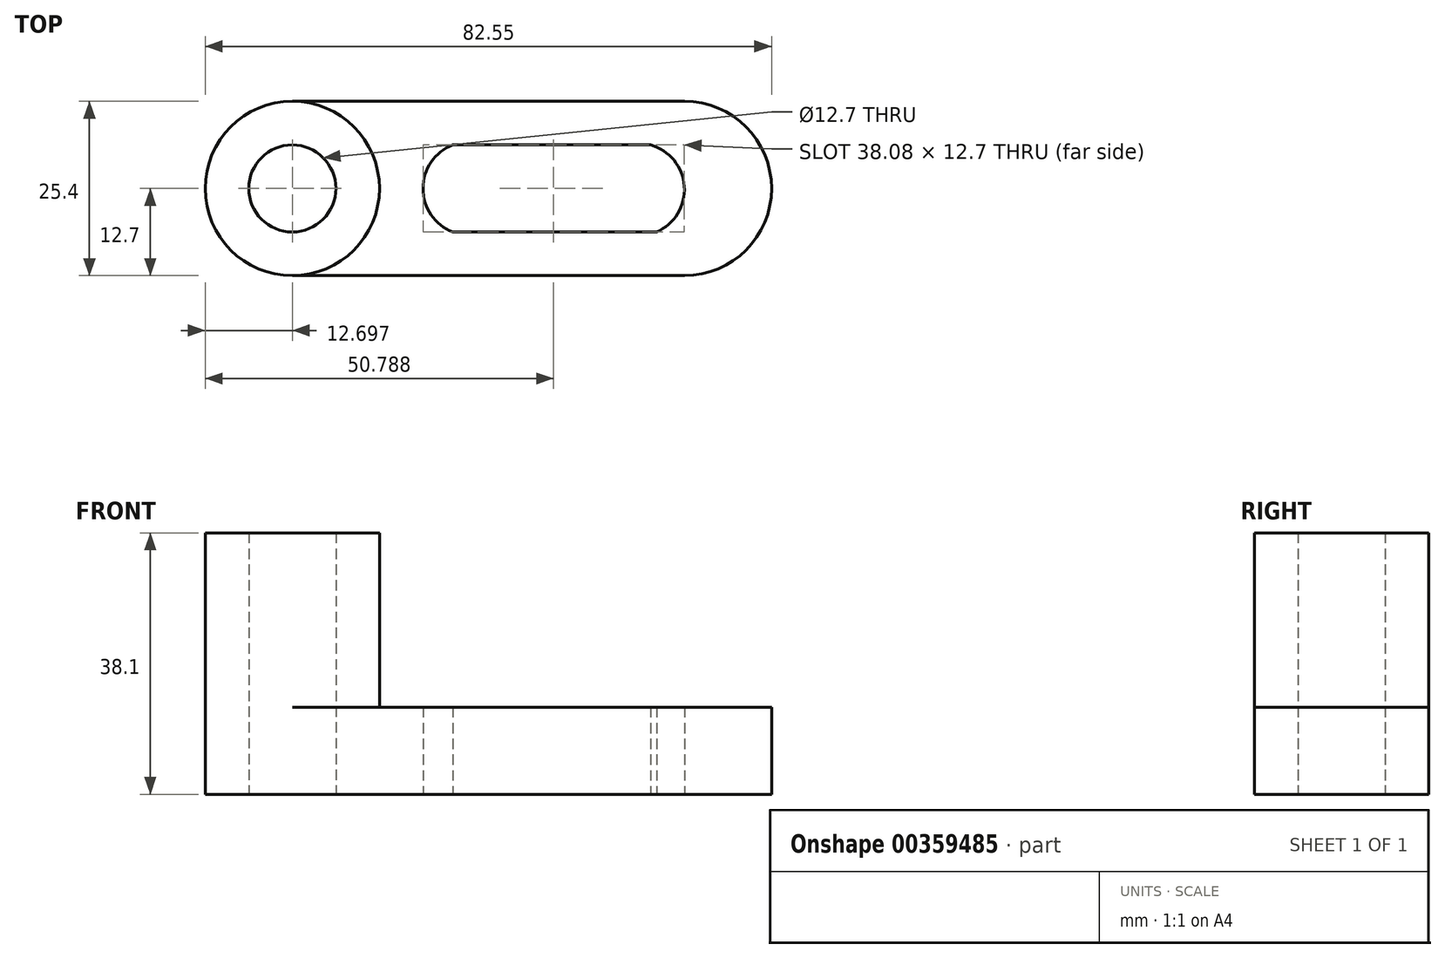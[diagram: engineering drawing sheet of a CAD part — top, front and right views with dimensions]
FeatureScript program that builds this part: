
annotation { "Feature Type Name" : "Feature", "Feature Type Description" : "" }
export const myFeature = defineFeature(function(context is Context, id is Id, definition is map)
    precondition{}
    {
        {
            var Q0;
            Q0=qCreatedBy(makeId("Front.planeOp"),FACE);
            var sketch = newSketch(context, id + "F0", { "sketchPlane" : qUnion([Q0])});
            skLineSegment(sketch, "E0", {"start": v(-36.1, 38.1) * mm, "end": v(-36.1, 0) * mm});
            skLineSegment(sketch, "E1", {"start": v(-36.1, 0) * mm, "end": v(46.46, 0) * mm});
            skLineSegment(sketch, "E2", {"start": v(46.46, 0) * mm, "end": v(46.46, 38.1) * mm});
            skLineSegment(sketch, "E3", {"start": v(46.46, 38.1) * mm, "end": v(-36.1, 38.1) * mm});
            skSolve(sketch);
        }
        {
            var Q0;
            Q0 = qSketchRegion(id + "F0", true);
            extrude(context, id + "F1", {"entities" : qUnion([Q0]), "oppositeDirection" : true, "depth" : 25.4 * mm});
        }
        {
            var Q0;
            Q0=qCreatedBy(makeId("Front.planeOp"),FACE);
            var sketch = newSketch(context, id + "F2", { "sketchPlane" : qUnion([Q0])});
            skLineSegment(sketch, "E4", {"start": v(-10.7, 38.1) * mm, "end": v(-10.7, 12.7) * mm});
            skLineSegment(sketch, "E5", {"start": v(-10.7, 12.7) * mm, "end": v(46.46, 12.7) * mm});
            skLineSegment(sketch, "E6", {"start": v(46.46, 12.7) * mm, "end": v(46.46, 38.1) * mm});
            skLineSegment(sketch, "E7", {"start": v(46.46, 38.1) * mm, "end": v(-10.7, 38.1) * mm});
            skSolve(sketch);
        }
        {
            var Q0;
            Q0 = qSketchRegion(id + "F2", true);
            extrude(context, id + "F3", {"entities" : qUnion([Q0]), "operationType" : NewBodyOperationType.REMOVE, "oppositeDirection" : true, "depth" : 25.4 * mm});
        }
        {
            var Q0;
            Q0=qCreatedBy(makeId("Top.planeOp"),FACE);
            var sketch = newSketch(context, id + "F4", { "sketchPlane" : qUnion([Q0])});
            skArc(sketch, "E8", {"start": v(33.76, 0) * mm, "mid": v(46.46, 12.7) * mm, "end": v(33.76, 25.4) * mm});
            skLineSegment(sketch, "E9", {"start": v(33.76, 25.4) * mm, "end": v(46.46, 25.4) * mm});
            skLineSegment(sketch, "E10", {"start": v(46.46, 25.4) * mm, "end": v(46.46, 0) * mm});
            skLineSegment(sketch, "E11", {"start": v(46.46, 0) * mm, "end": v(33.76, 0) * mm});
            skSolve(sketch);
        }
        {
            var Q0;
            Q0 = qSketchRegion(id + "F4", true);
            extrude(context, id + "F5", {"entities" : qUnion([Q0]), "operationType" : NewBodyOperationType.REMOVE, "depth" : 25.4 * mm});
        }
        {
            var Q0;
            Q0=qCreatedBy(makeId("Top.planeOp"),FACE);
            var sketch = newSketch(context, id + "F6", { "sketchPlane" : qUnion([Q0])});
            skArc(sketch, "E12", {"start": v(0, 19.05) * mm, "mid": v(-4.34, 12.7) * mm, "end": v(0, 6.35) * mm});
            skArc(sketch, "E13", {"start": v(29.7, 6.35) * mm, "mid": v(33.74, 13.01) * mm, "end": v(28.82, 19.05) * mm});
            skLineSegment(sketch, "E14", {"start": v(0, 19.05) * mm, "end": v(28.82, 19.05) * mm});
            skLineSegment(sketch, "E15", {"start": v(29.7, 6.35) * mm, "end": v(0, 6.35) * mm});
            skSolve(sketch);
        }
        {
            var Q0;
            Q0 = qSketchRegion(id + "F6", true);
            extrude(context, id + "F7", {"entities" : qUnion([Q0]), "operationType" : NewBodyOperationType.REMOVE, "depth" : 25.4 * mm});
        }
        {
            var Q0;
            Q0=makeQuery(id+"F1.opExtrude","CAP_FACE",FACE,{"disambiguationData":[OSD([sQuery(id+"F0.wireOp",EDGE,"E0"),sQuery(id+"F0.wireOp",EDGE,"E1"),sQuery(id+"F0.wireOp",EDGE,"E2"),sQuery(id+"F0.wireOp",EDGE,"E3")])],"isStart":true});
            var sketch = newSketch(context, id + "F8", { "sketchPlane" : qUnion([Q0])});
            skLineSegment(sketch, "E16", {"start": v(-36.1, 12.7) * mm, "end": v(-10.7, 12.7) * mm});
            skLineSegment(sketch, "E17", {"start": v(-10.7, 12.7) * mm, "end": v(-10.7, 38.1) * mm});
            skLineSegment(sketch, "E18", {"start": v(-10.7, 38.1) * mm, "end": v(-36.1, 38.1) * mm});
            skLineSegment(sketch, "E19", {"start": v(-36.1, 38.1) * mm, "end": v(-36.1, 12.7) * mm});
            skSolve(sketch);
        }
        {
            var Q0;
            Q0 = qSketchRegion(id + "F8", true);
            extrude(context, id + "F9", {"entities" : qUnion([Q0]), "operationType" : NewBodyOperationType.REMOVE, "oppositeDirection" : true, "depth" : 25.4 * mm});
        }
        {
            var Q0;
            Q0=makeQuery(id+"F9.boolean.opBoolean","MERGE",FACE,{"derivedFrom":[makeQuery(id+"F3.boolean.opBoolean","COPY",FACE,{"derivedFrom":makeQuery(id+"F3.opExtrude","SWEPT_FACE",FACE,{"disambiguationData":[OSD([sQuery(id+"F2.wireOp",EDGE,"E5")])]})}),makeQuery(id+"F9.opExtrude","SWEPT_FACE",FACE,{"disambiguationData":[OSD([sQuery(id+"F8.wireOp",EDGE,"E16")])]})]});
            var sketch = newSketch(context, id + "F10", { "sketchPlane" : qUnion([Q0])});
            skCircle(sketch, "E20", {"center": v(-23.4, 12.7) * mm, "radius": 12.7 * mm});
            skSolve(sketch);
        }
        {
            var Q0;
            Q0 = qSketchRegion(id + "F10", true);
            extrude(context, id + "F11", {"entities" : qUnion([Q0]), "operationType" : NewBodyOperationType.ADD, "depth" : 25.4 * mm});
        }
        {
            var Q0;
            Q0=qCreatedBy(makeId("Top.planeOp"),FACE);
            var sketch = newSketch(context, id + "F12", { "sketchPlane" : qUnion([Q0])});
            skCircle(sketch, "E21", {"center": v(-23.4, 12.7) * mm, "radius": 6.35 * mm});
            skSolve(sketch);
        }
        {
            var Q0;
            Q0 = qSketchRegion(id + "F12", true);
            extrude(context, id + "F13", {"entities" : qUnion([Q0]), "operationType" : NewBodyOperationType.REMOVE, "depth" : 38.1 * mm});
        }
        {
            var Q0;
            {var subQ0=makeQuery(id+"F9.opExtrude","SWEPT_FACE",FACE,{"disambiguationData":[OSD([sQuery(id+"F8.wireOp",EDGE,"E16")])]});var subQ1=sQuery(id+"F0.wireOp",EDGE,"E0");var subQ2=makeQuery(id+"F3.boolean.opBoolean","COPY",FACE,{"derivedFrom":makeQuery(id+"F3.opExtrude","SWEPT_FACE",FACE,{"disambiguationData":[OSD([sQuery(id+"F2.wireOp",EDGE,"E5")])]})});Q0=makeQuery(id+"F11.boolean.opBoolean","SPLIT",FACE,{"disambiguationData":[TD([makeQuery(id+"F1.opExtrude","SWEPT_FACE",FACE,{"disambiguationData":[OSD([subQ1])]}),makeQuery(id+"F1.opExtrude","CAP_FACE",FACE,{"disambiguationData":[OSD([subQ1,sQuery(id+"F0.wireOp",EDGE,"E1"),sQuery(id+"F0.wireOp",EDGE,"E2"),sQuery(id+"F0.wireOp",EDGE,"E3")])],"isStart":false}),subQ2,subQ0,makeQuery(id+"F11.opExtrude","SWEPT_FACE",FACE,{"disambiguationData":[OSD([sQuery(id+"F10.wireOp",EDGE,"E20")])]})])],"derivedFrom":makeQuery(id+"F9.boolean.opBoolean","MERGE",FACE,{"derivedFrom":[subQ2,subQ0]})});}
            var Q1;
            {var subQ0=makeQuery(id+"F9.opExtrude","SWEPT_FACE",FACE,{"disambiguationData":[OSD([sQuery(id+"F8.wireOp",EDGE,"E16")])]});var subQ1=sQuery(id+"F0.wireOp",EDGE,"E0");var subQ2=makeQuery(id+"F3.boolean.opBoolean","COPY",FACE,{"derivedFrom":makeQuery(id+"F3.opExtrude","SWEPT_FACE",FACE,{"disambiguationData":[OSD([sQuery(id+"F2.wireOp",EDGE,"E5")])]})});Q1=makeQuery(id+"F11.boolean.opBoolean","SPLIT",FACE,{"disambiguationData":[TD([makeQuery(id+"F1.opExtrude","SWEPT_FACE",FACE,{"disambiguationData":[OSD([subQ1])]}),makeQuery(id+"F1.opExtrude","CAP_FACE",FACE,{"disambiguationData":[OSD([subQ1,sQuery(id+"F0.wireOp",EDGE,"E1"),sQuery(id+"F0.wireOp",EDGE,"E2"),sQuery(id+"F0.wireOp",EDGE,"E3")])],"isStart":true}),subQ2,subQ0,makeQuery(id+"F11.opExtrude","SWEPT_FACE",FACE,{"disambiguationData":[OSD([sQuery(id+"F10.wireOp",EDGE,"E20")])]})])],"derivedFrom":makeQuery(id+"F9.boolean.opBoolean","MERGE",FACE,{"derivedFrom":[subQ2,subQ0]})});}
            extrude(context, id + "F14", {"entities" : qUnion([Q0, Q1]), "operationType" : NewBodyOperationType.REMOVE, "oppositeDirection" : true, "depth" : 25.4 * mm});
        }
    });
